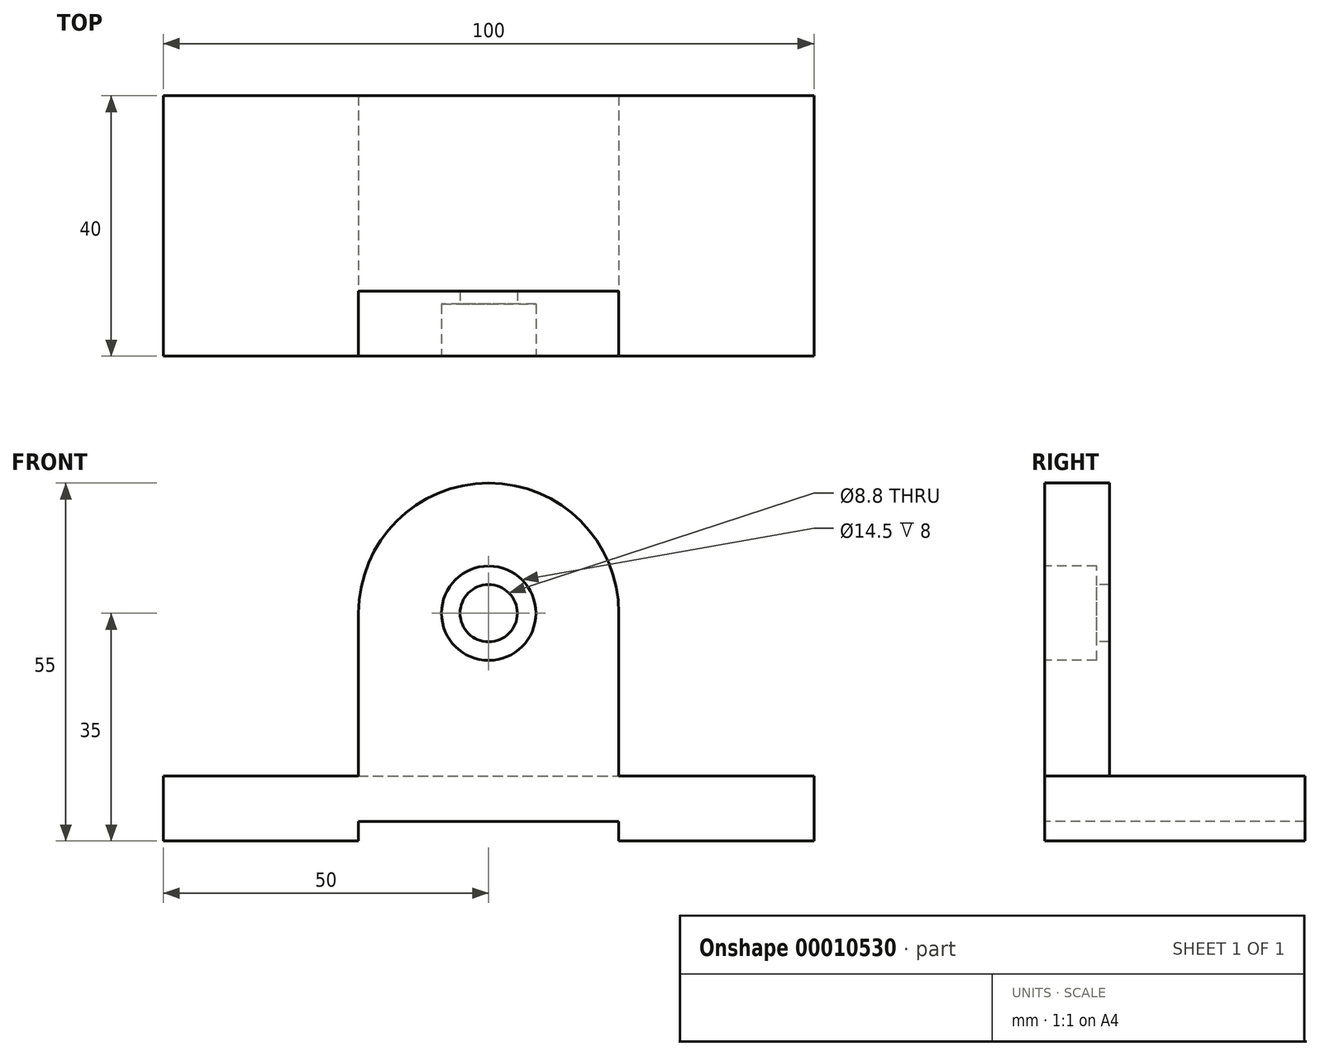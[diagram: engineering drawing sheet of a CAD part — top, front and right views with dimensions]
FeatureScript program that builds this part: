
annotation { "Feature Type Name" : "Feature", "Feature Type Description" : "" }
export const myFeature = defineFeature(function(context is Context, id is Id, definition is map)
    precondition{}
    {
        {
            var Q0;
            Q0=qCreatedBy(makeId("Top.planeOp"),FACE);
            var sketch = newSketch(context, id + "F0", { "sketchPlane" : qUnion([Q0])});
            skLineSegment(sketch, "E0.bottom", {"start": v(0, 0) * mm, "end": v(100, 0) * mm});
            skLineSegment(sketch, "E0.top", {"start": v(0, 40) * mm, "end": v(100, 40) * mm});
            skLineSegment(sketch, "E0.left", {"start": v(0, 0) * mm, "end": v(0, 40) * mm});
            skLineSegment(sketch, "E0.right", {"start": v(100, 0) * mm, "end": v(100, 40) * mm});
            skSolve(sketch);
        }
        {
            var Q0;
            Q0=qSketchRegion(id+"F0",true);
            extrude(context, id + "F1", {"entities" : qUnion([Q0]), "depth" : 10 * mm});
        }
        {
            var Q0;
            Q0=makeQuery(id+"F1.opExtrude","SWEPT_FACE",FACE,{"disambiguationData":[OSD([sQuery(id+"F0.wireOp",EDGE,"E0.bottom")])]});
            var sketch = newSketch(context, id + "F2", { "sketchPlane" : qUnion([Q0])});
            skLineSegment(sketch, "E1", {"start": v(30, 0) * mm, "end": v(30, 35) * mm});
            skArc(sketch, "E2", {"start": v(30, 35) * mm, "mid": v(50, 55) * mm, "end": v(70, 35) * mm});
            skLineSegment(sketch, "E3", {"start": v(70, 35) * mm, "end": v(70, 0) * mm});
            skLineSegment(sketch, "E4", {"start": v(70, 0) * mm, "end": v(30, 0) * mm});
            skSolve(sketch);
        }
        {
            var Q0;
            Q0=qSketchRegion(id+"F2",true);
            extrude(context, id + "F3", {"entities" : qUnion([Q0]), "operationType" : NewBodyOperationType.ADD, "oppositeDirection" : true, "depth" : 10 * mm});
        }
        {
            var Q0;
            Q0=makeQuery(id+"F3.boolean.opBoolean","MERGE",FACE,{"derivedFrom":[makeQuery(id+"F1.opExtrude","SWEPT_FACE",FACE,{"disambiguationData":[OSD([sQuery(id+"F0.wireOp",EDGE,"E0.bottom")])]}),makeQuery(id+"F3.opExtrude","CAP_FACE",FACE,{"disambiguationData":[OSD([sQuery(id+"F2.wireOp",EDGE,"E1"),sQuery(id+"F2.wireOp",EDGE,"E2"),sQuery(id+"F2.wireOp",EDGE,"E3"),sQuery(id+"F2.wireOp",EDGE,"E4")])],"isStart":true})]});
            var sketch = newSketch(context, id + "F4", { "sketchPlane" : qUnion([Q0])});
            skLineSegment(sketch, "E5.bottom", {"start": v(30, 0) * mm, "end": v(70, 0) * mm});
            skLineSegment(sketch, "E5.top", {"start": v(30, 3) * mm, "end": v(70, 3) * mm});
            skLineSegment(sketch, "E5.left", {"start": v(30, 0) * mm, "end": v(30, 3) * mm});
            skLineSegment(sketch, "E5.right", {"start": v(70, 0) * mm, "end": v(70, 3) * mm});
            skSolve(sketch);
        }
        {
            var Q0;
            Q0=qSketchRegion(id+"F4",true);
            extrude(context, id + "F5", {"entities" : qUnion([Q0]), "operationType" : NewBodyOperationType.REMOVE, "endBound" : BoundingType.THROUGH_ALL, "oppositeDirection" : true, "depth" : 25 * mm});
        }
        {
            var Q0;
            Q0=makeQuery(id+"F3.boolean.opBoolean","MERGE",FACE,{"derivedFrom":[makeQuery(id+"F1.opExtrude","SWEPT_FACE",FACE,{"disambiguationData":[OSD([sQuery(id+"F0.wireOp",EDGE,"E0.bottom")])]}),makeQuery(id+"F3.opExtrude","CAP_FACE",FACE,{"disambiguationData":[OSD([sQuery(id+"F2.wireOp",EDGE,"E1"),sQuery(id+"F2.wireOp",EDGE,"E2"),sQuery(id+"F2.wireOp",EDGE,"E3"),sQuery(id+"F2.wireOp",EDGE,"E4")])],"isStart":true})]});
            var sketch = newSketch(context, id + "F6", { "sketchPlane" : qUnion([Q0])});
            skCircle(sketch, "E6", {"center": v(50, 35) * mm, "radius": 4.4 * mm});
            skSolve(sketch);
        }
        {
            var Q0;
            Q0=qSketchRegion(id+"F6",true);
            extrude(context, id + "F7", {"entities" : qUnion([Q0]), "operationType" : NewBodyOperationType.REMOVE, "endBound" : BoundingType.THROUGH_ALL, "oppositeDirection" : true, "depth" : 25 * mm});
        }
        {
            var Q0;
            Q0=makeQuery(id+"F3.boolean.opBoolean","MERGE",FACE,{"derivedFrom":[makeQuery(id+"F1.opExtrude","SWEPT_FACE",FACE,{"disambiguationData":[OSD([sQuery(id+"F0.wireOp",EDGE,"E0.bottom")])]}),makeQuery(id+"F3.opExtrude","CAP_FACE",FACE,{"disambiguationData":[OSD([sQuery(id+"F2.wireOp",EDGE,"E1"),sQuery(id+"F2.wireOp",EDGE,"E2"),sQuery(id+"F2.wireOp",EDGE,"E3"),sQuery(id+"F2.wireOp",EDGE,"E4")])],"isStart":true})]});
            var sketch = newSketch(context, id + "F8", { "sketchPlane" : qUnion([Q0])});
            skCircle(sketch, "E7", {"center": v(50, 35) * mm, "radius": 7.25 * mm});
            skSolve(sketch);
        }
        {
            var Q0;
            Q0=qSketchRegion(id+"F8",true);
            extrude(context, id + "F9", {"entities" : qUnion([Q0]), "operationType" : NewBodyOperationType.REMOVE, "oppositeDirection" : true, "depth" : 8 * mm});
        }
    });
